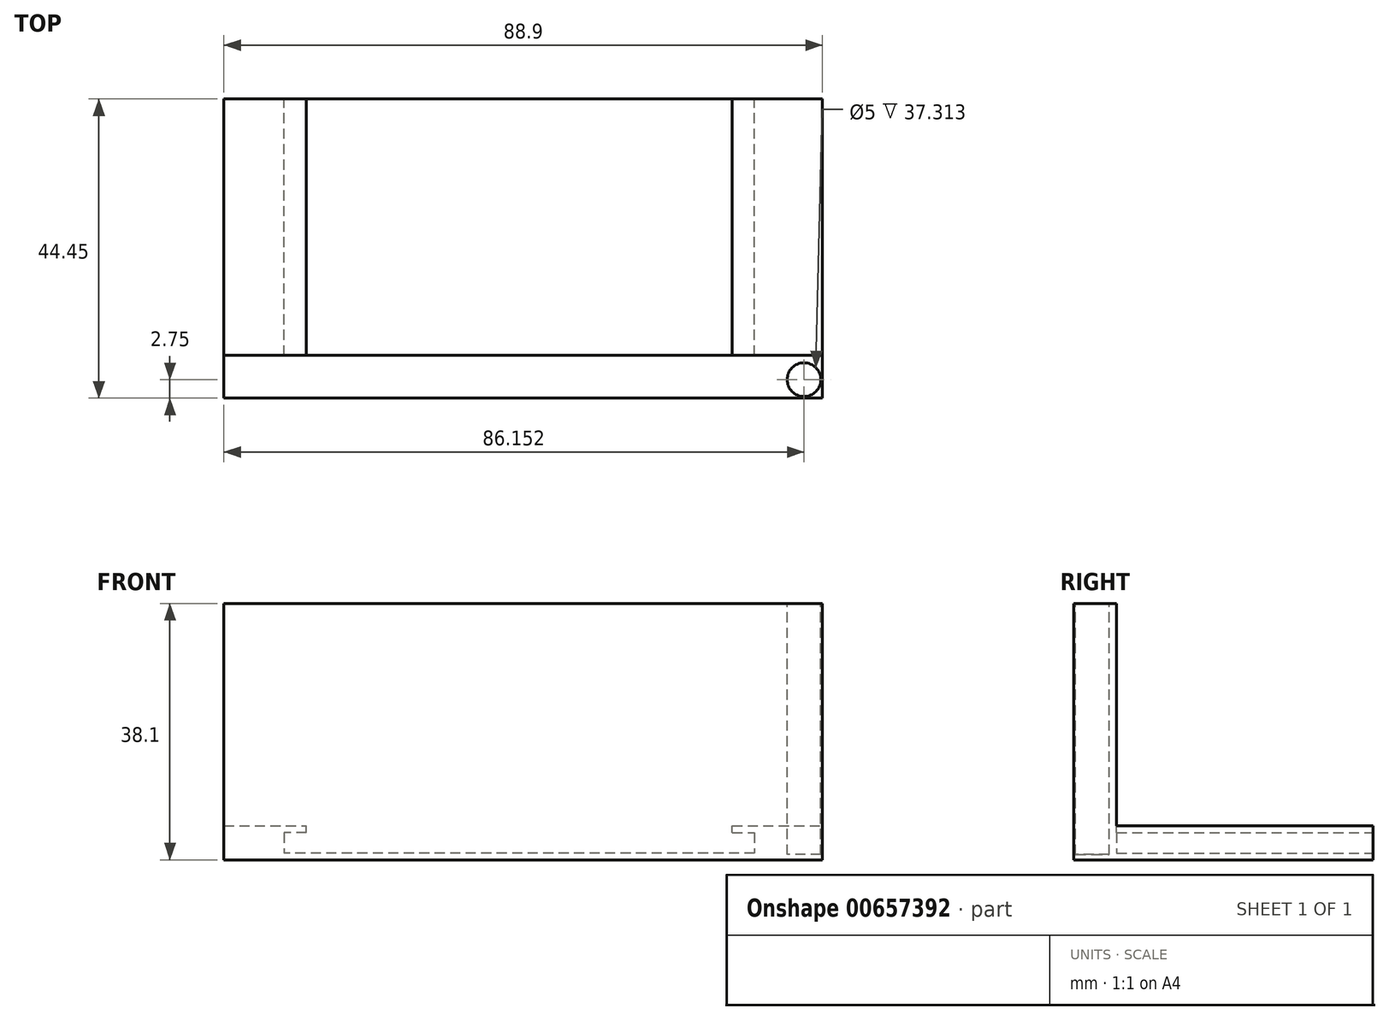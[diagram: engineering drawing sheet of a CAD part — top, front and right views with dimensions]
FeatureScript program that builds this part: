
annotation { "Feature Type Name" : "Feature", "Feature Type Description" : "" }
export const myFeature = defineFeature(function(context is Context, id is Id, definition is map)
    precondition{}
    {
        {
            var Q0;
            Q0=qCreatedBy(makeId("Front.planeOp"),FACE);
            var sketch = newSketch(context, id + "F0", { "sketchPlane" : qUnion([Q0])});
            skLineSegment(sketch, "E0.bottom", {"start": v(44.7, -18.22) * mm, "end": v(-44.2, -18.22) * mm});
            skLineSegment(sketch, "E0.top", {"start": v(44.7, 19.88) * mm, "end": v(-44.2, 19.88) * mm});
            skLineSegment(sketch, "E0.left", {"start": v(44.7, -18.22) * mm, "end": v(44.7, 19.88) * mm});
            skLineSegment(sketch, "E0.right", {"start": v(-44.2, -18.22) * mm, "end": v(-44.2, 19.88) * mm});
            skSolve(sketch);
        }
        {
            var Q0;
            Q0 = qSketchRegion(id + "F0", true);
            extrude(context, id + "F1", {"entities" : qUnion([Q0]), "depth" : 44.45 * mm, "offsetDistance" : 25.4 * mm});
        }
        {
            var Q0;
            Q0=makeQuery(id+"F1.opExtrude","SWEPT_FACE",FACE,{"disambiguationData":[OSD([sQuery(id+"F0.wireOp",EDGE,"E0.left")])]});
            var sketch = newSketch(context, id + "F2", { "sketchPlane" : qUnion([Q0])});
            skLineSegment(sketch, "E1.bottom", {"start": v(0, 19.88) * mm, "end": v(-38.1, 19.88) * mm});
            skLineSegment(sketch, "E1.top", {"start": v(0, -13.14) * mm, "end": v(-38.1, -13.14) * mm});
            skLineSegment(sketch, "E1.left", {"start": v(0, 19.88) * mm, "end": v(0, -13.14) * mm});
            skLineSegment(sketch, "E1.right", {"start": v(-38.1, 19.88) * mm, "end": v(-38.1, -13.14) * mm});
            skSolve(sketch);
        }
        {
            var Q0;
            Q0 = qSketchRegion(id + "F2", true);
            extrude(context, id + "F3", {"entities" : qUnion([Q0]), "operationType" : NewBodyOperationType.REMOVE, "endBound" : BoundingType.THROUGH_ALL, "oppositeDirection" : true, "depth" : 225.3 * mm, "offsetDistance" : 25.4 * mm});
        }
        {
            var Q0;
            Q0=makeQuery(id+"F1.opExtrude","SWEPT_FACE",FACE,{"disambiguationData":[OSD([sQuery(id+"F0.wireOp",EDGE,"E0.top")])]});
            var sketch = newSketch(context, id + "F4", { "sketchPlane" : qUnion([Q0])});
            skLineSegment(sketch, "E2.bottom", {"start": v(44.7, -44.45) * mm, "end": v(39.2, -44.45) * mm});
            skLineSegment(sketch, "E2.top", {"start": v(44.7, -38.95) * mm, "end": v(39.2, -38.95) * mm});
            skLineSegment(sketch, "E2.left", {"start": v(44.7, -44.45) * mm, "end": v(44.7, -38.95) * mm});
            skLineSegment(sketch, "E2.right", {"start": v(39.2, -44.45) * mm, "end": v(39.2, -38.95) * mm});
            skSolve(sketch);
        }
        {
            var Q0;
            Q0 = qSketchRegion(id + "F4", true);
            extrude(context, id + "F5", {"entities" : qUnion([Q0]), "operationType" : NewBodyOperationType.ADD, "oppositeDirection" : true, "depth" : 36.07 * mm, "offsetDistance" : 25.4 * mm});
        }
        {
            var Q0;
            Q0=makeQuery(id+"F5.boolean.opBoolean","MERGE",FACE,{"derivedFrom":[makeQuery(id+"F1.opExtrude","SWEPT_FACE",FACE,{"disambiguationData":[OSD([sQuery(id+"F0.wireOp",EDGE,"E0.top")])]}),makeQuery(id+"F5.opExtrude","CAP_FACE",FACE,{"disambiguationData":[OSD([sQuery(id+"F4.wireOp",EDGE,"E2.bottom"),sQuery(id+"F4.wireOp",EDGE,"E2.top"),sQuery(id+"F4.wireOp",EDGE,"E2.left"),sQuery(id+"F4.wireOp",EDGE,"E2.right")])],"isStart":true})]});
            var sketch = newSketch(context, id + "F6", { "sketchPlane" : qUnion([Q0])});
            skLineSegment(sketch, "E3", {"start": v(39.2, -38.95) * mm, "end": v(44.7, -44.45) * mm, "construction": true});
            skLineSegment(sketch, "E4", {"start": v(44.7, -44.45) * mm, "end": v(44.7, -38.95) * mm, "construction": true});
            skLineSegment(sketch, "E5", {"start": v(44.7, -38.95) * mm, "end": v(39.2, -44.45) * mm, "construction": true});
            skCircle(sketch, "E6", {"center": v(41.95, -41.7) * mm, "radius": 2.5 * mm});
            skSolve(sketch);
        }
        {
            var Q0;
            Q0 = qSketchRegion(id + "F6", true);
            extrude(context, id + "F7", {"entities" : qUnion([Q0]), "operationType" : NewBodyOperationType.REMOVE, "oppositeDirection" : true, "depth" : 37.31 * mm, "offsetDistance" : 25.4 * mm, "hasSecondDirection" : true, "secondDirectionOppositeDirection" : false, "secondDirectionDepth" : 1 * mm});
        }
        {
            var Q0;
            Q0=makeQuery(id+"F1.opExtrude","CAP_FACE",FACE,{"disambiguationData":[OSD([sQuery(id+"F0.wireOp",EDGE,"E0.bottom"),sQuery(id+"F0.wireOp",EDGE,"E0.top"),sQuery(id+"F0.wireOp",EDGE,"E0.left"),sQuery(id+"F0.wireOp",EDGE,"E0.right")])],"isStart":true});
            var sketch = newSketch(context, id + "F8", { "sketchPlane" : qUnion([Q0])});
            skLineSegment(sketch, "E7", {"start": v(0, 23.5) * mm, "end": v(0, -24.26) * mm, "construction": true});
            skLineSegment(sketch, "E8", {"start": v(-44.7, -15.68) * mm, "end": v(54.34, -15.68) * mm, "construction": true});
            skPoint(sketch, "E8.endSnap0", {"position": v(44.2, -15.68) * mm});
            skLineSegment(sketch, "E9.top", {"start": v(-34.6, -17.23) * mm, "end": v(35.24, -17.23) * mm});
            skLineSegment(sketch, "E10.0", {"start": v(-44.7, -17.18) * mm, "end": v(54.34, -17.18) * mm, "construction": true});
            skLineSegment(sketch, "E11.MirrorCS", {"start": v(-44.7, -14.18) * mm, "end": v(-31.3, -14.18) * mm, "construction": true});
            skLineSegment(sketch, "E12", {"start": v(35.24, -14.2) * mm, "end": v(35.24, -17.23) * mm});
            skLineSegment(sketch, "E13", {"start": v(-34.6, -14.2) * mm, "end": v(-34.6, -17.23) * mm});
            skLineSegment(sketch, "E14", {"start": v(-31.3, -14.18) * mm, "end": v(-31.3, -13.14) * mm});
            skLineSegment(sketch, "E15", {"start": v(31.94, -14.18) * mm, "end": v(31.94, -13.14) * mm});
            skLineSegment(sketch, "E16.trimOffspring", {"start": v(31.94, -14.18) * mm, "end": v(54.34, -14.18) * mm, "construction": true});
            skLineSegment(sketch, "E17", {"start": v(31.94, -14.18) * mm, "end": v(35.24, -14.2) * mm});
            skLineSegment(sketch, "E18", {"start": v(31.94, -13.14) * mm, "end": v(-31.3, -13.14) * mm});
            skLineSegment(sketch, "E19", {"start": v(-31.3, -14.18) * mm, "end": v(-34.6, -14.2) * mm});
            skSolve(sketch);
        }
        {
            var Q0;
            Q0 = qSketchRegion(id + "F8", true);
            extrude(context, id + "F9", {"entities" : qUnion([Q0]), "operationType" : NewBodyOperationType.REMOVE, "oppositeDirection" : true, "depth" : 38.1 * mm, "offsetDistance" : 25.4 * mm});
        }
    });
